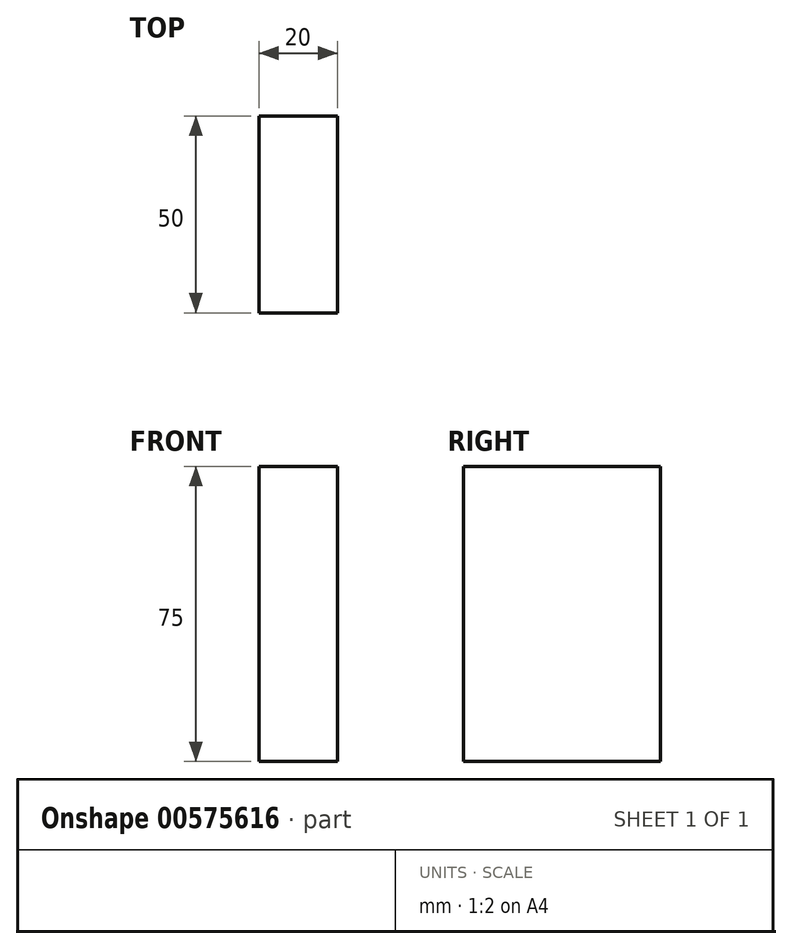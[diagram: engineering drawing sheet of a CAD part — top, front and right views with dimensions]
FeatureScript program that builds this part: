
annotation { "Feature Type Name" : "Feature", "Feature Type Description" : "" }
export const myFeature = defineFeature(function(context is Context, id is Id, definition is map)
    precondition{}
    {
        {
            var Q0;
            Q0=qCreatedBy(makeId("Top.planeOp"),FACE);
            var sketch = newSketch(context, id + "F0", { "sketchPlane" : qUnion([Q0])});
            skLineSegment(sketch, "E0.bottom", {"start": v(0, 0) * mm, "end": v(20, 0) * mm});
            skLineSegment(sketch, "E0.top", {"start": v(0, 50) * mm, "end": v(20, 50) * mm});
            skLineSegment(sketch, "E0.left", {"start": v(0, 0) * mm, "end": v(0, 50) * mm});
            skLineSegment(sketch, "E0.right", {"start": v(20, 0) * mm, "end": v(20, 50) * mm});
            skSolve(sketch);
        }
        {
            var Q0;
            Q0=makeQuery(id+"F0.imprint","IMPRINT",FACE,{"disambiguationData":[TD([[makeQuery(id+"F0.imprint","IMPRINT",EDGE,{"derivedFrom":sQuery(id+"F0.wireOp",EDGE,"E0.bottom")}),1.0]])]});
            extrude(context, id + "F1", {"entities" : qUnion([Q0]), "depth" : 75 * mm, "offsetDistance" : 25 * mm});
        }
    });
